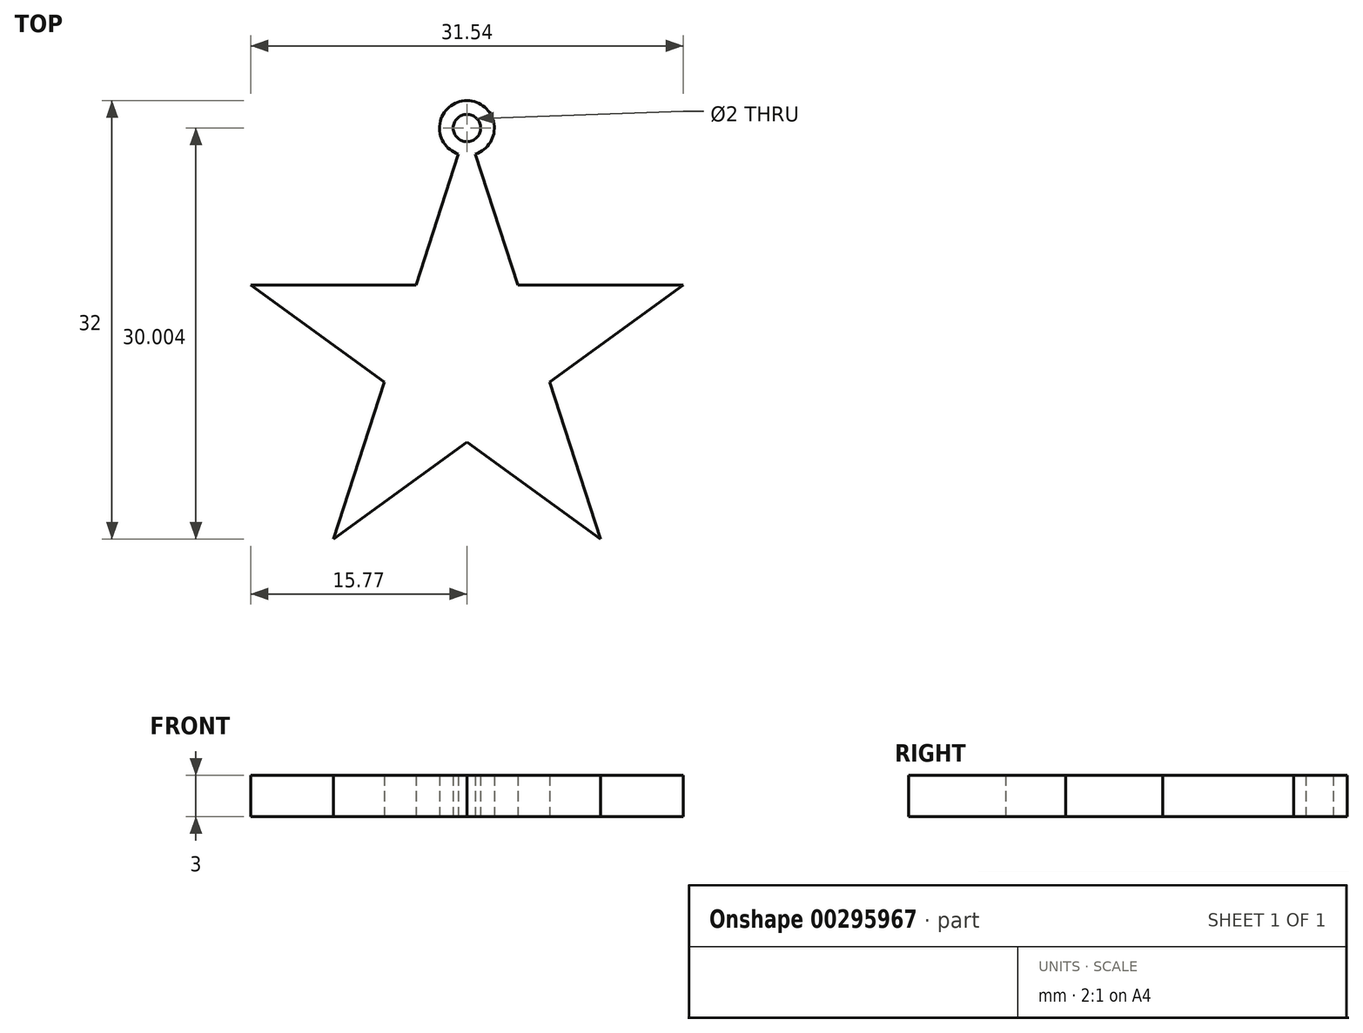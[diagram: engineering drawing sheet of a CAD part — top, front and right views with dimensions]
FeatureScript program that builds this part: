
annotation { "Feature Type Name" : "Feature", "Feature Type Description" : "" }
export const myFeature = defineFeature(function(context is Context, id is Id, definition is map)
    precondition{}
    {
        {
            var Q0;
            Q0=qCreatedBy(makeId("Top.planeOp"),FACE);
            var sketch = newSketch(context, id + "F0", { "sketchPlane" : qUnion([Q0])});
            skCircle(sketch, "E0.cCircle", {"center": v(0, 0) * mm, "radius": 13.42 * mm, "construction": true});
            skLineSegment(sketch, "E0.0", {"start": v(0, 16.58) * mm, "end": v(15.77, 5.12) * mm});
            skLineSegment(sketch, "E0.1", {"start": v(15.77, 5.12) * mm, "end": v(9.75, -13.42) * mm});
            skLineSegment(sketch, "E0.2", {"start": v(9.75, -13.42) * mm, "end": v(-9.75, -13.42) * mm});
            skLineSegment(sketch, "E0.3", {"start": v(-9.75, -13.42) * mm, "end": v(-15.77, 5.12) * mm});
            skLineSegment(sketch, "E0.4", {"start": v(-15.77, 5.12) * mm, "end": v(0, 16.58) * mm});
            skPoint(sketch, "E0.0.midPoint", {"position": v(7.89, 10.85) * mm});
            skPoint(sketch, "E1.orphan", {"position": v(-7.89, 10.85) * mm});
            skPoint(sketch, "E2.trimOffspring.end.orphan", {"position": v(-12.76, -4.15) * mm});
            skPoint(sketch, "E3.trimOffspring.end.orphan", {"position": v(12.76, -4.15) * mm});
            skPoint(sketch, "E4.orphan", {"position": v(0, -13.42) * mm});
            skLineSegment(sketch, "E5", {"start": v(0, 16.58) * mm, "end": v(-3.72, 5.12) * mm});
            skLineSegment(sketch, "E6", {"start": v(-15.77, 5.12) * mm, "end": v(-3.72, 5.12) * mm});
            skLineSegment(sketch, "E7", {"start": v(15.77, 5.12) * mm, "end": v(6.02, -1.96) * mm});
            skLineSegment(sketch, "E8", {"start": v(9.75, -13.42) * mm, "end": v(0, -6.33) * mm});
            skLineSegment(sketch, "E9", {"start": v(9.75, -13.42) * mm, "end": v(6.02, -1.96) * mm});
            skLineSegment(sketch, "E10.trimOffspring", {"start": v(3.72, 5.12) * mm, "end": v(15.77, 5.12) * mm});
            skLineSegment(sketch, "E11.trimOffspring", {"start": v(3.72, 5.12) * mm, "end": v(0, 16.58) * mm});
            skLineSegment(sketch, "E12.trimOffspring", {"start": v(0, -6.33) * mm, "end": v(-9.75, -13.42) * mm});
            skLineSegment(sketch, "E13.trimOffspring", {"start": v(-6.02, -1.96) * mm, "end": v(-15.77, 5.12) * mm});
            skLineSegment(sketch, "E14.trimOffspring", {"start": v(-6.02, -1.96) * mm, "end": v(-9.75, -13.42) * mm});
            skCircle(sketch, "E15", {"center": v(0, 16.58) * mm, "radius": 2 * mm});
            skCircle(sketch, "E16", {"center": v(0, 16.58) * mm, "radius": 1 * mm});
            skSolve(sketch);
        }
        {
            var Q0;
            Q0=makeQuery(id+"F0.imprint","IMPRINT",FACE,{"disambiguationData":[TD([[makeQuery(id+"F0.imprint","IMPRINT",EDGE,{"derivedFrom":sQuery(id+"F0.wireOp",EDGE,"XSsLThOJ-ZaQI-v7Vn-JERq-CprFEK3kPXpU")}),1.0]])]});
            var Q1;
            {var subQ4=sQuery(id+"F0.wireOp",EDGE,"E6");Q1=makeQuery(id+"F0.imprint","IMPRINT",FACE,{"disambiguationData":[TD([[makeQuery(id+"F0.imprint","IMPRINT",EDGE,{"derivedFrom":subQ4}),-1.0]])]});}
            var Q2;
            {var subQ0=sQuery(id+"F0.wireOp",EDGE,"E16");var subQ1=sQuery(id+"F0.wireOp",EDGE,"E5");var subQ2=makeQuery(id+"F0.imprint","INTERSECT",VERTEX,{"derivedFrom":[subQ1,subQ0]});Q2=makeQuery(id+"F0.imprint","IMPRINT",FACE,{"disambiguationData":[TD([[makeQuery(id+"F0.imprint","IMPRINT",EDGE,{"disambiguationData":[TD([[subQ2,-1.0]])],"derivedFrom":subQ1}),1.0]])]});}
            var Q3;
            {var subQ0=sQuery(id+"F0.wireOp",EDGE,"E15");var subQ1=sQuery(id+"F0.wireOp",EDGE,"E0.0");var subQ2=makeQuery(id+"F0.imprint","INTERSECT",VERTEX,{"derivedFrom":[subQ1,subQ0]});Q3=makeQuery(id+"F0.imprint","IMPRINT",FACE,{"disambiguationData":[TD([[makeQuery(id+"F0.imprint","IMPRINT",EDGE,{"disambiguationData":[TD([[subQ2,1.0]])],"derivedFrom":subQ1}),-1.0]])]});}
            var Q4;
            {var subQ0=sQuery(id+"F0.wireOp",EDGE,"E15");var subQ1=sQuery(id+"F0.wireOp",EDGE,"E0.0");var subQ2=makeQuery(id+"F0.imprint","INTERSECT",VERTEX,{"derivedFrom":[subQ1,subQ0]});Q4=makeQuery(id+"F0.imprint","IMPRINT",FACE,{"disambiguationData":[TD([[makeQuery(id+"F0.imprint","IMPRINT",EDGE,{"disambiguationData":[TD([[subQ2,1.0]])],"derivedFrom":subQ1}),1.0]])]});}
            var Q5;
            {var subQ0=sQuery(id+"F0.wireOp",EDGE,"E15");var subQ1=sQuery(id+"F0.wireOp",EDGE,"E0.4");var subQ2=makeQuery(id+"F0.imprint","INTERSECT",VERTEX,{"derivedFrom":[subQ1,subQ0]});Q5=makeQuery(id+"F0.imprint","IMPRINT",FACE,{"disambiguationData":[TD([[makeQuery(id+"F0.imprint","IMPRINT",EDGE,{"disambiguationData":[TD([[subQ2,-1.0]])],"derivedFrom":subQ1}),-1.0]])]});}
            extrude(context, id + "F1", {"entities" : qUnion([Q0, Q1, Q2, Q3, Q4, Q5]), "depth" : 3 * mm});
        }
    });
